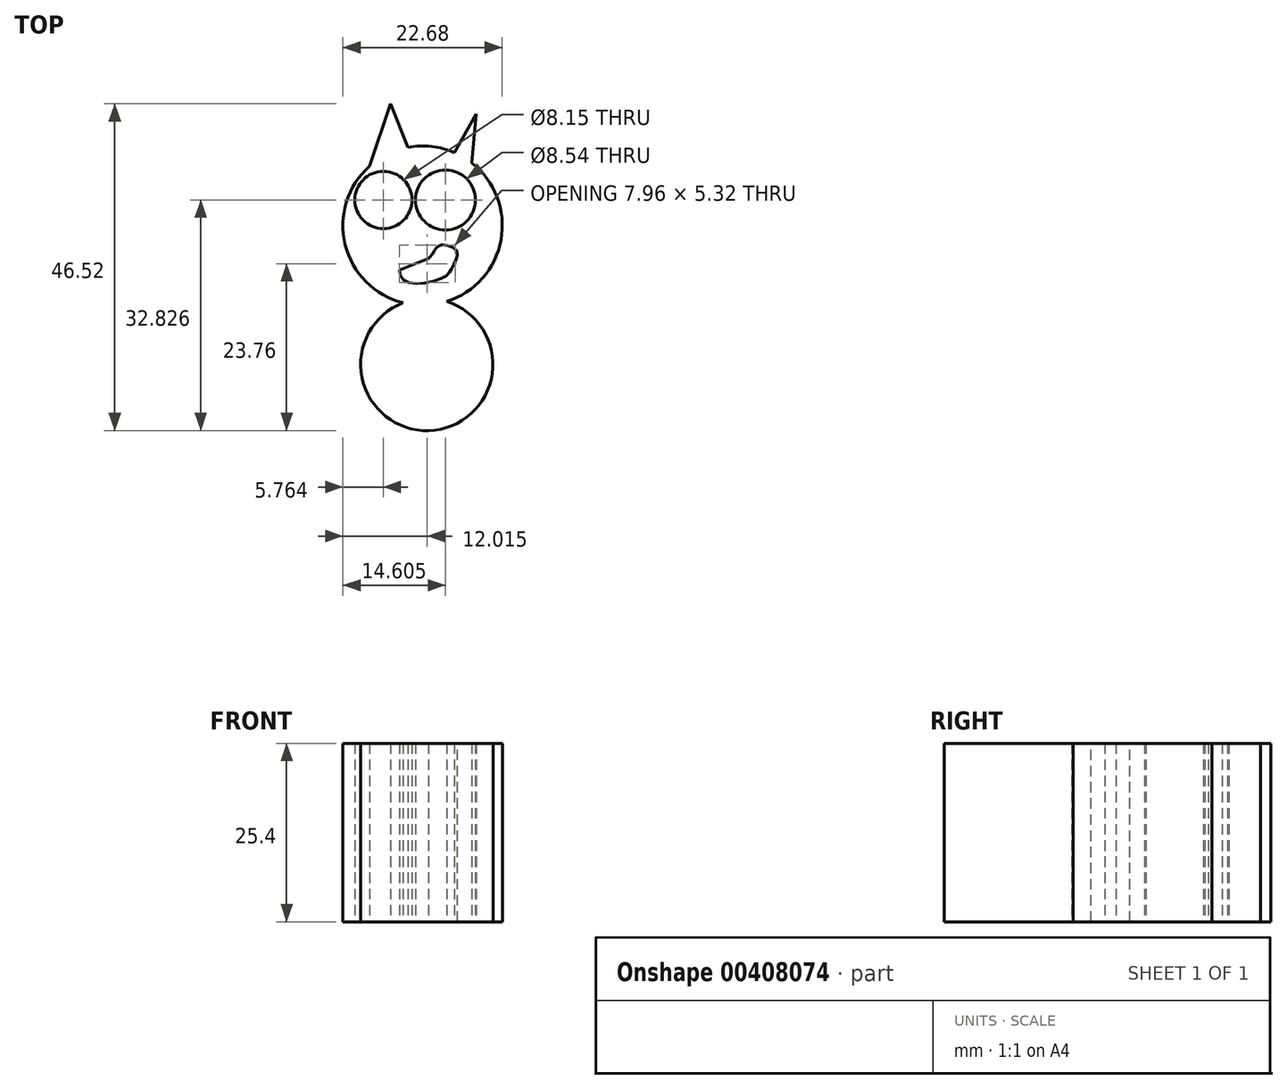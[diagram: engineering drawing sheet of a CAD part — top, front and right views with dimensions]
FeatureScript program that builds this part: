
annotation { "Feature Type Name" : "Feature", "Feature Type Description" : "" }
export const myFeature = defineFeature(function(context is Context, id is Id, definition is map)
    precondition{}
    {
        {
            var Q0;
            Q0=qCreatedBy(makeId("Top.planeOp"),FACE);
            var sketch = newSketch(context, id + "F0", { "sketchPlane" : qUnion([Q0])});
            skCircle(sketch, "E0", {"center": v(-14.35, 49.88) * mm, "radius": 11.34 * mm});
            skCircle(sketch, "E1", {"center": v(-19.93, 53.53) * mm, "radius": 4.07 * mm});
            skCircle(sketch, "E2", {"center": v(-11.09, 53.53) * mm, "radius": 4.27 * mm});
            skFitSpline(sketch, "E3", {"points": [v(-17.7, 44.69) * mm, v(-16.78, 41.94) * mm, v(-11.3, 42.55) * mm, v(-10.07, 44.08) * mm, v(-9.47, 46.22) * mm, v(-11.6, 47.13) * mm, v(-12.52, 46.52) * mm, v(-13.12, 45.6) * mm, v(-13.73, 45) * mm], "startDerivative": vector(0.1, -22.93) * mm, "endDerivative": vector(-7.8, -6.87) * mm});
            skFitSpline(sketch, "E4", {"points": [v(-13.52, 45.18) * mm, v(-17.7, 43.56) * mm], "startDerivative": vector(-4.17, -1.63) * mm, "endDerivative": vector(-4.17, -1.63) * mm});
            skPoint(sketch, "E5.endSnap0", {"position": v(9.06, 36.56) * mm});
            skPoint(sketch, "E5.end.orphan", {"position": v(21.64, 36.56) * mm});
            skPoint(sketch, "E6.end.orphan", {"position": v(11.58, 32.49) * mm});
            skPoint(sketch, "E6.start.orphan", {"position": v(0, 25.3) * mm});
            skPoint(sketch, "E7.end.orphan", {"position": v(6.54, 40.63) * mm});
            skLineSegment(sketch, "E8", {"start": v(3.65, 36.15) * mm, "end": v(3.65, 36.43) * mm});
            skLineSegment(sketch, "E9", {"start": v(3.65, 36.43) * mm, "end": v(9.06, 36.56) * mm});
            skLineSegment(sketch, "E10", {"start": v(-21.9, 57.09) * mm, "end": v(-21.9, 58.34) * mm});
            skPoint(sketch, "E11.endSnap0", {"position": v(-7.34, 64.16) * mm});
            skPoint(sketch, "E11.end.orphan", {"position": v(-7.34, 58.8) * mm});
            skPoint(sketch, "E12.orphan", {"position": v(-18.9, 60.27) * mm});
            skPoint(sketch, "E13.orphan", {"position": v(-4.87, 68.04) * mm});
            skPoint(sketch, "E14.start.orphan", {"position": v(-9.8, 60.27) * mm});
            skLineSegment(sketch, "E15", {"start": v(-21.9, 58.34) * mm, "end": v(-18.9, 67.29) * mm});
            skLineSegment(sketch, "E16", {"start": v(-18.95, 67.29) * mm, "end": v(-16.44, 61.03) * mm});
            skLineSegment(sketch, "E17", {"start": v(-6.75, 65.77) * mm, "end": v(-7.34, 58.8) * mm});
            skLineSegment(sketch, "E18", {"start": v(-6.75, 65.77) * mm, "end": v(-9.8, 60.27) * mm});
            skCircle(sketch, "E19", {"center": v(-13.75, 30.1) * mm, "radius": 9.4 * mm});
            skPoint(sketch, "E20.end.orphan", {"position": v(-31.06, 39.8) * mm});
            skPoint(sketch, "E21.end.orphan", {"position": v(-38.42, 39.8) * mm});
            skPoint(sketch, "E21.start.orphan", {"position": v(-33.23, 36.43) * mm});
            skPoint(sketch, "E22.orphan", {"position": v(3.65, 39.8) * mm});
            skSolve(sketch);
        }
        {
            var Q0;
            Q0 = qSketchRegion(id + "F0", true);
            extrude(context, id + "F1", {"entities" : qUnion([Q0]), "depth" : 25.4 * mm});
        }
    });
